# Revit family: Shower-Showerarm-KOHLER-BEITOU-K-22307T
name_source: partatom
category: Plumbing Fixtures
revit_build: Autodesk Revit 2017 (Build: 20160225_1515(x64)
units: mm (PartAtom-declared; Revit-internal decimal feet)

## family parameters
Cut with Voids When Loaded = No
Host = Face
OmniClass Number = 23.31.25.00
OmniClass Title = Toilet and Bath Specialties
Part Type = Normal
Room Calculation Point = No
Round Connector Dimension = Use Diameter
Shared = No

## types (1)
- CP-Polished Chrome
    ADA Compliant = No
    Assembly Code = D2010700
    CW Connection = No
    Cold Water Inlet = Cold Water Inlet
    Date Modified = 09/20/2020
    Default Elevation = 72"
    Description = Wall mount shower arm
    Drain Included = No
    Finish = Kohler-Metal-CP-Polished_Chrome
    Flow Rate = 0 GPM
    HW Connection = Yes
    Height = 1 3/4"
    Hot Water Inlet = Hot Water Inlet
    Length = 18 3/16"
    Manufacturer = KOHLER Co.
    Master Format 2014 = 22 42 23
    Master Format 2014 Name = Residential Showers
    Material = Premium Metal Construction
    Model = K-22307T-CP
    Pressure = 0.00 psi
    Product Documentation Link = https://files.kohler.com.cn
    Product Name = BEITOU
    Product Page URL = https://www.kohler.com.cn
    Tempered Water Inlet = Tempered Water Inlet
    Type = 1
    URL = http://www.kohler.com.cn
    Vent Connection = No
    Waste Connection = No
    Waste Water Outlet = Waste Water Outlet
    WaterSense Certified = No
    Width = 2 3/8"

## geometry (parser evidence)
native form markers: Sweep x5
no freeform markers — native parametric forms only
